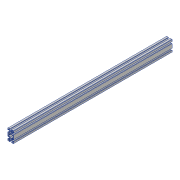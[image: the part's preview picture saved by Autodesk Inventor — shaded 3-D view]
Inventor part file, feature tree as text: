
AUTODESK INVENTOR PART (.ipt)
format: ipt  version: 2018 (Build 220112000, 112)  size: 241,664 bytes
history: native  units: mm
features: extrude x1, sketch x1
ambient origin geometry x8: Origin, YZ Plane, XZ Plane, XY Plane, X Axis, Y Axis, Z Axis, Center Point
bodies: Solid1 (feature_tree)
feature tree (2):
  extrude  "Extrusion1"  [1 undecoded]
  sketch  "Sketch1"  dims[d0=560.0mm d1=0.0mm]
note: 1 required parameter value undecoded (feature->parameter linkage not recoverable at this tier; creation-order binding heuristic only, values carry confidence <= 0.55)
